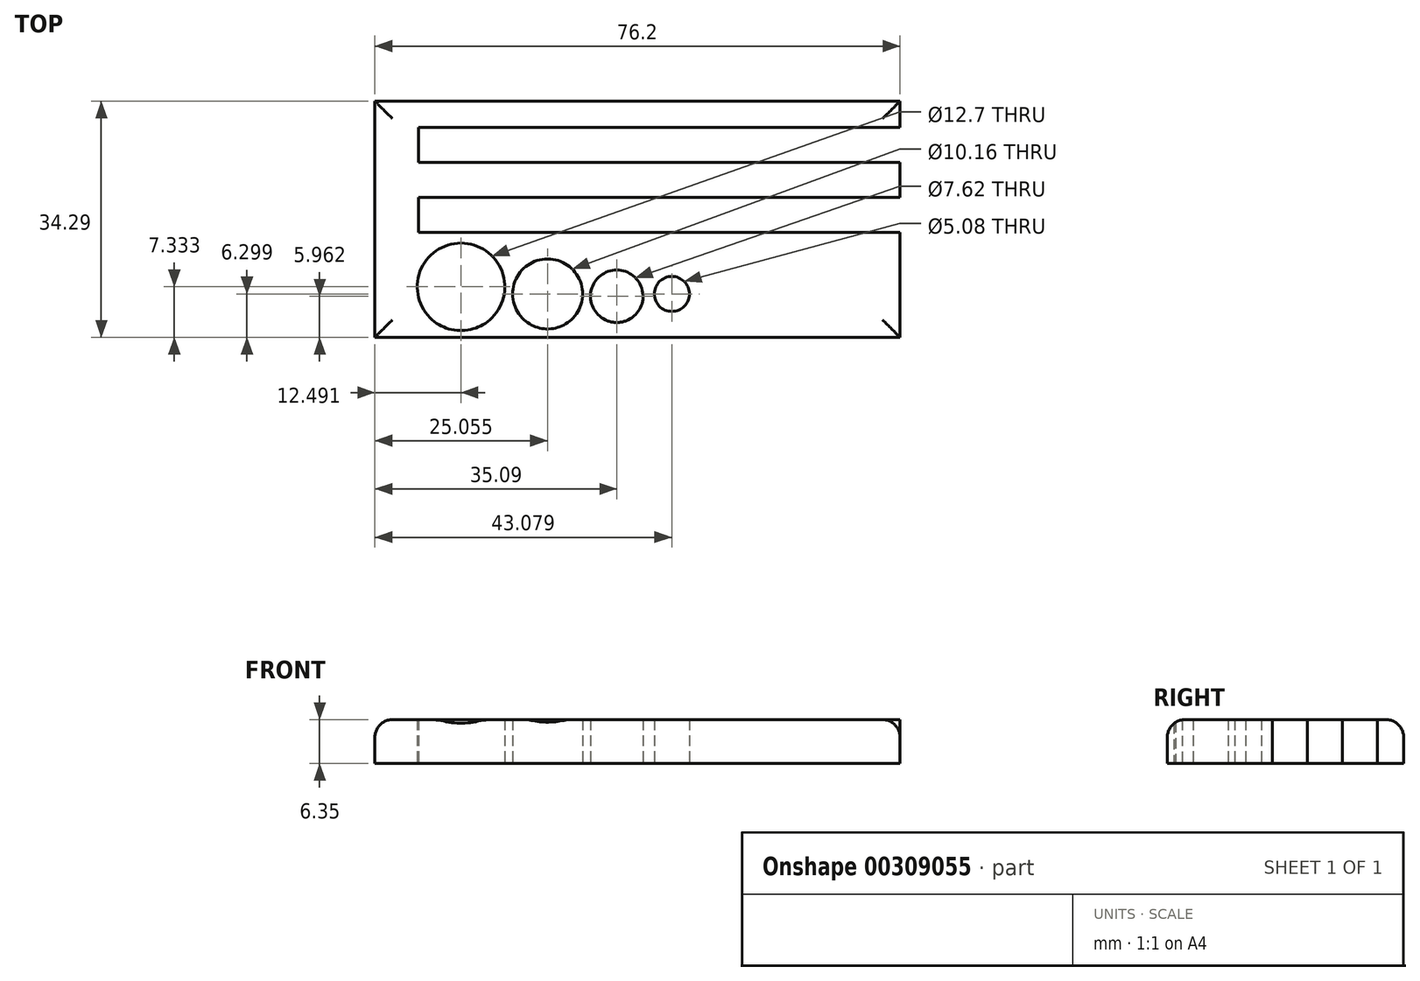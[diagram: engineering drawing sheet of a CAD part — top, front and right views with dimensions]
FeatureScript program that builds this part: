
annotation { "Feature Type Name" : "Feature", "Feature Type Description" : "" }
export const myFeature = defineFeature(function(context is Context, id is Id, definition is map)
    precondition{}
    {
        {
            var Q0;
            Q0=qCreatedBy(makeId("Top.planeOp"),FACE);
            var sketch = newSketch(context, id + "F0", { "sketchPlane" : qUnion([Q0])});
            skLineSegment(sketch, "E0.bottom", {"start": v(-73.62, 2.13) * mm, "end": v(-149.82, 2.13) * mm});
            skLineSegment(sketch, "E0.top", {"start": v(-73.62, 36.42) * mm, "end": v(-149.82, 36.42) * mm});
            skLineSegment(sketch, "E0.left", {"start": v(-73.62, 2.13) * mm, "end": v(-73.62, 36.42) * mm});
            skLineSegment(sketch, "E0.right", {"start": v(-149.82, 2.13) * mm, "end": v(-149.82, 36.42) * mm});
            skPoint(sketch, "E0.middle", {"position": v(-111.72, 19.27) * mm});
            skLineSegment(sketch, "E1.bottom", {"start": v(-73.62, 27.53) * mm, "end": v(-143.47, 27.53) * mm});
            skLineSegment(sketch, "E1.top", {"start": v(-73.62, 32.6) * mm, "end": v(-143.47, 32.6) * mm});
            skLineSegment(sketch, "E1.left", {"start": v(-73.62, 27.53) * mm, "end": v(-73.62, 32.6) * mm});
            skLineSegment(sketch, "E1.right", {"start": v(-143.47, 27.53) * mm, "end": v(-143.47, 32.6) * mm});
            skPoint(sketch, "E1.middle", {"position": v(-108.55, 30.07) * mm});
            skLineSegment(sketch, "E2.bottom", {"start": v(-73.62, 22.45) * mm, "end": v(-143.47, 22.45) * mm});
            skLineSegment(sketch, "E2.top", {"start": v(-73.62, 17.37) * mm, "end": v(-143.47, 17.37) * mm});
            skLineSegment(sketch, "E2.left", {"start": v(-73.62, 17.37) * mm, "end": v(-73.62, 22.45) * mm});
            skLineSegment(sketch, "E2.right", {"start": v(-143.47, 17.37) * mm, "end": v(-143.47, 22.45) * mm});
            skCircle(sketch, "E3", {"center": v(-137.33, 9.46) * mm, "radius": 6.35 * mm});
            skCircle(sketch, "E4", {"center": v(-124.76, 8.43) * mm, "radius": 5.08 * mm});
            skCircle(sketch, "E5", {"center": v(-114.73, 8.1) * mm, "radius": 3.81 * mm});
            skCircle(sketch, "E6", {"center": v(-106.74, 8.43) * mm, "radius": 2.54 * mm});
            skSolve(sketch);
        }
        {
            var Q0;
            {var subQ1=sQuery(id+"F0.wireOp",EDGE,"E0.bottom");Q0=makeQuery(id+"F0.imprint","IMPRINT",FACE,{"disambiguationData":[TD([[makeQuery(id+"F0.imprint","IMPRINT",EDGE,{"derivedFrom":subQ1}),-1.0]])]});}
            extrude(context, id + "F1", {"entities" : qUnion([Q0]), "depth" : 6.35 * mm});
        }
        {
            var Q0;
            Q0=makeQuery(id+"F1.opExtrude","CAP_EDGE",EDGE,{"disambiguationData":[OSD([sQuery(id+"F0.wireOp",EDGE,"E0.top")])],"isStart":false});
            var Q1;
            Q1=makeQuery(id+"F1.opExtrude","CAP_EDGE",EDGE,{"disambiguationData":[OSD([sQuery(id+"F0.wireOp",EDGE,"E0.right")])],"isStart":false});
            var Q2;
            Q2=makeQuery(id+"F1.opExtrude","CAP_EDGE",EDGE,{"disambiguationData":[OSD([sQuery(id+"F0.wireOp",EDGE,"E0.bottom")])],"isStart":false});
            var Q3;
            {var subQ0=sQuery(id+"F0.wireOp",EDGE,"E0.left");Q3=makeQuery(id+"F1.opExtrude","CAP_EDGE",EDGE,{"disambiguationData":[OSD([subQ0]),TDD([makeQuery(id+"F0.imprint","IMPRINT",EDGE,{"disambiguationData":[TD([[makeQuery(id+"F0.imprint","INTERSECT",VERTEX,{"derivedFrom":[sQuery(id+"F0.wireOp",EDGE,"E0.bottom"),subQ0]}),-1.0]])],"derivedFrom":subQ0})])],"isStart":false});}
            var Q4;
            {var subQ0=sQuery(id+"F0.wireOp",EDGE,"E0.left");Q4=makeQuery(id+"F1.opExtrude","CAP_EDGE",EDGE,{"disambiguationData":[OSD([subQ0]),TDD([makeQuery(id+"F0.imprint","IMPRINT",EDGE,{"disambiguationData":[TD([[makeQuery(id+"F0.imprint","INTERSECT",VERTEX,{"derivedFrom":[sQuery(id+"F0.wireOp",EDGE,"E0.top"),subQ0]}),1.0]])],"derivedFrom":subQ0})])],"isStart":false});}
            fillet(context, id + "F2", {"entities" : qUnion([Q0, Q1, Q2, Q3, Q4]), "radius" : 2.54 * mm, "tangentPropagation" : true, "allowEdgeOverflow" : false});
        }
    });
